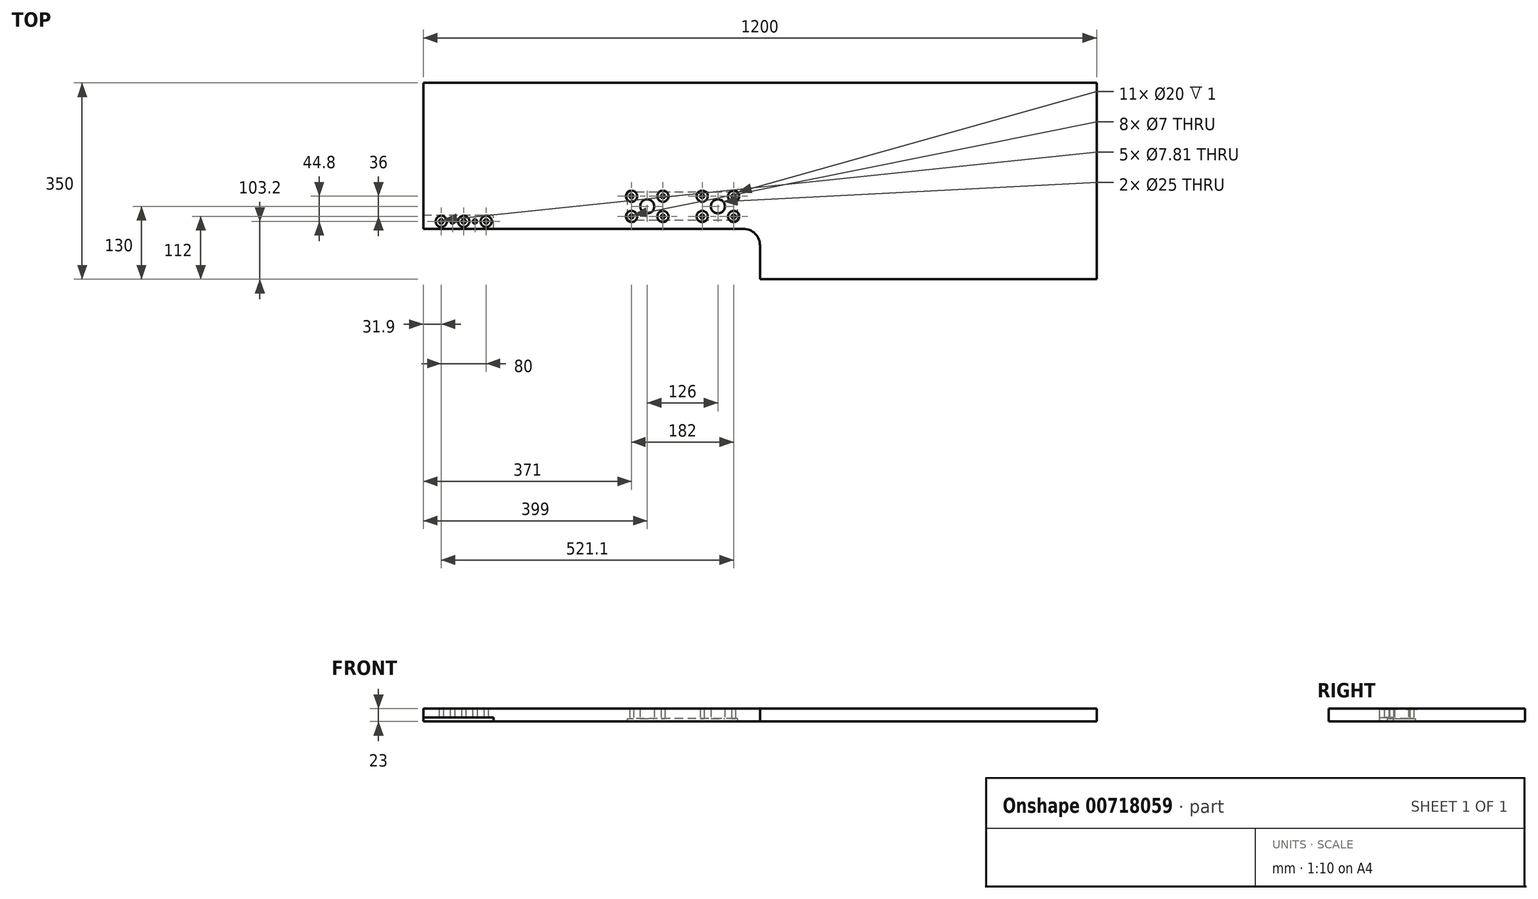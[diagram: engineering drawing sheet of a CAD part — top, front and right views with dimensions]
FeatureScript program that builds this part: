
annotation { "Feature Type Name" : "Feature", "Feature Type Description" : "" }
export const myFeature = defineFeature(function(context is Context, id is Id, definition is map)
    precondition{}
    {
        {
            var Q0;
            Q0=qCreatedBy(makeId("Top.planeOp"),FACE);
            var sketch = newSketch(context, id + "F0", { "sketchPlane" : qUnion([Q0])});
            skLineSegment(sketch, "E0.bottom", {"start": v(600, 0) * mm, "end": v(1200, 0) * mm});
            skLineSegment(sketch, "E0.top", {"start": v(0, 350) * mm, "end": v(1200, 350) * mm});
            skLineSegment(sketch, "E0.right", {"start": v(1200, 0) * mm, "end": v(1200, 350) * mm});
            skLineSegment(sketch, "E1.top", {"start": v(0, 90) * mm, "end": v(570, 90) * mm});
            skLineSegment(sketch, "E1.right", {"start": v(600, 0) * mm, "end": v(600, 60) * mm});
            skLineSegment(sketch, "E2", {"start": v(0, 90) * mm, "end": v(0, 350) * mm});
            skLineSegment(sketch, "E3", {"start": v(0, 0) * mm, "end": v(600, 0) * mm, "construction": true});
            skLineSegment(sketch, "E4", {"start": v(0, 0) * mm, "end": v(0, 90) * mm, "construction": true});
            skPoint(sketch, "E5.visualSharp", {"position": v(600, 90) * mm});
            skArc(sketch, "E5.filletArc", {"start": v(600, 60) * mm, "mid": v(591.21, 81.21) * mm, "end": v(570, 90) * mm});
            skSolve(sketch);
        }
        {
            var Q0;
            Q0=qSketchRegion(id+"F0",true);
            var Q1;
            Q1=makeQuery(id+"F0.imprint","IMPRINT",FACE,{"disambiguationData":[TD([[makeQuery(id+"F0.imprint","IMPRINT",EDGE,{"derivedFrom":sQuery(id+"F0.wireOp",EDGE,"E0.bottom")}),1.0]])]});
            extrude(context, id + "F1", {"entities" : qUnion([Q0, Q1]), "depth" : 18 * mm, "offsetDistance" : 25 * mm});
        }
        {
            var Q0;
            Q0=makeQuery(id+"F1.opExtrude","CAP_FACE",FACE,{"disambiguationData":[OSD([sQuery(id+"F0.wireOp",EDGE,"E0.bottom"),sQuery(id+"F0.wireOp",EDGE,"E0.top"),sQuery(id+"F0.wireOp",EDGE,"E0.right"),sQuery(id+"F0.wireOp",EDGE,"E1.top"),sQuery(id+"F0.wireOp",EDGE,"E1.right"),sQuery(id+"F0.wireOp",EDGE,"E2"),sQuery(id+"F0.wireOp",EDGE,"E5.filletArc")])],"isStart":true});
            var sketch = newSketch(context, id + "F2", { "sketchPlane" : qUnion([Q0])});
            skLineSegment(sketch, "E6.bottom", {"start": v(555, -105) * mm, "end": v(369, -105) * mm});
            skLineSegment(sketch, "E6.top", {"start": v(555, -155) * mm, "end": v(369, -155) * mm});
            skLineSegment(sketch, "E6.left", {"start": v(560, -110) * mm, "end": v(560, -150) * mm});
            skLineSegment(sketch, "E6.right", {"start": v(364, -110) * mm, "end": v(364, -150) * mm});
            skPoint(sketch, "E7.visualSharp", {"position": v(560, -155) * mm});
            skArc(sketch, "E7.filletArc", {"start": v(555, -155) * mm, "mid": v(558.54, -153.54) * mm, "end": v(560, -150) * mm});
            skPoint(sketch, "E8.visualSharp", {"position": v(364, -155) * mm});
            skArc(sketch, "E8.filletArc", {"start": v(364, -150) * mm, "mid": v(365.46, -153.54) * mm, "end": v(369, -155) * mm});
            skPoint(sketch, "E9.visualSharp", {"position": v(364, -105) * mm});
            skArc(sketch, "E9.filletArc", {"start": v(369, -105) * mm, "mid": v(365.46, -106.46) * mm, "end": v(364, -110) * mm});
            skPoint(sketch, "E10.visualSharp", {"position": v(560, -105) * mm});
            skArc(sketch, "E10.filletArc", {"start": v(560, -110) * mm, "mid": v(558.54, -106.46) * mm, "end": v(555, -105) * mm});
            skSolve(sketch);
        }
        {
            var Q0;
            Q0=makeQuery(id+"F2.imprint","IMPRINT",FACE,{"disambiguationData":[TD([[makeQuery(id+"F2.imprint","IMPRINT",EDGE,{"derivedFrom":sQuery(id+"F2.wireOp",EDGE,"E6.bottom")}),-1.0]])]});
            extrude(context, id + "F3", {"entities" : qUnion([Q0]), "operationType" : NewBodyOperationType.ADD, "depth" : 5 * mm, "offsetDistance" : 25 * mm});
        }
        {
            var Q0;
            Q0=makeQuery(id+"F3.opExtrude","CAP_FACE",FACE,{"disambiguationData":[OSD([sQuery(id+"F0.wireOp",EDGE,"E0.bottom"),sQuery(id+"F0.wireOp",EDGE,"E0.top"),sQuery(id+"F0.wireOp",EDGE,"E0.right"),sQuery(id+"F0.wireOp",EDGE,"E1.top"),sQuery(id+"F0.wireOp",EDGE,"E1.right"),sQuery(id+"F0.wireOp",EDGE,"E2"),sQuery(id+"F0.wireOp",EDGE,"E5.filletArc"),sQuery(id+"F2.wireOp",EDGE,"E6.bottom"),sQuery(id+"F2.wireOp",EDGE,"E6.top"),sQuery(id+"F2.wireOp",EDGE,"E6.left"),sQuery(id+"F2.wireOp",EDGE,"E6.right")])],"isStart":false});
            var sketch = newSketch(context, id + "F4", { "sketchPlane" : qUnion([Q0])});
            skLineSegment(sketch, "E11.bottom", {"start": v(0, -90) * mm, "end": v(125, -90) * mm});
            skLineSegment(sketch, "E11.top", {"start": v(0, -114.8) * mm, "end": v(120, -114.8) * mm});
            skLineSegment(sketch, "E11.left", {"start": v(0, -90) * mm, "end": v(0, -114.8) * mm});
            skLineSegment(sketch, "E11.right", {"start": v(125, -90) * mm, "end": v(125, -109.8) * mm});
            skPoint(sketch, "E12.visualSharp", {"position": v(125, -114.8) * mm});
            skArc(sketch, "E12.filletArc", {"start": v(120, -114.8) * mm, "mid": v(123.54, -113.34) * mm, "end": v(125, -109.8) * mm});
            skSolve(sketch);
        }
        {
            var Q0;
            Q0=makeQuery(id+"F4.imprint","IMPRINT",FACE,{"disambiguationData":[TD([[makeQuery(id+"F4.imprint","IMPRINT",EDGE,{"derivedFrom":sQuery(id+"F4.wireOp",EDGE,"E11.bottom")}),-1.0]])]});
            extrude(context, id + "F5", {"entities" : qUnion([Q0]), "operationType" : NewBodyOperationType.REMOVE, "oppositeDirection" : true, "depth" : 7 * mm, "offsetDistance" : 25 * mm});
        }
        {
            var Q0;
            Q0=makeQuery(id+"F1.opExtrude","CAP_FACE",FACE,{"disambiguationData":[OSD([sQuery(id+"F0.wireOp",EDGE,"E0.bottom"),sQuery(id+"F0.wireOp",EDGE,"E0.top"),sQuery(id+"F0.wireOp",EDGE,"E0.right"),sQuery(id+"F0.wireOp",EDGE,"E1.top"),sQuery(id+"F0.wireOp",EDGE,"E1.right"),sQuery(id+"F0.wireOp",EDGE,"E2"),sQuery(id+"F0.wireOp",EDGE,"E5.filletArc")])],"isStart":true});
            var sketch = newSketch(context, id + "F6", { "sketchPlane" : qUnion([Q0])});
            skCircle(sketch, "E13", {"center": v(525, -130) * mm, "radius": 12.5 * mm});
            skCircle(sketch, "E14", {"center": v(399, -130) * mm, "radius": 12.5 * mm});
            skLineSegment(sketch, "E15", {"start": v(399, -130) * mm, "end": v(525, -130) * mm, "construction": true});
            skLineSegment(sketch, "E16.bottom", {"start": v(427, -112) * mm, "end": v(371, -112) * mm, "construction": true});
            skLineSegment(sketch, "E16.top", {"start": v(427, -148) * mm, "end": v(371, -148) * mm, "construction": true});
            skLineSegment(sketch, "E16.left", {"start": v(427, -112) * mm, "end": v(427, -148) * mm, "construction": true});
            skLineSegment(sketch, "E16.right", {"start": v(371, -112) * mm, "end": v(371, -148) * mm, "construction": true});
            skLineSegment(sketch, "E17.bottom", {"start": v(553, -112) * mm, "end": v(497, -112) * mm, "construction": true});
            skLineSegment(sketch, "E17.top", {"start": v(553, -148) * mm, "end": v(497, -148) * mm, "construction": true});
            skLineSegment(sketch, "E17.left", {"start": v(553, -112) * mm, "end": v(553, -148) * mm, "construction": true});
            skLineSegment(sketch, "E17.right", {"start": v(497, -112) * mm, "end": v(497, -148) * mm, "construction": true});
            skCircle(sketch, "E18", {"center": v(371, -112) * mm, "radius": 3.5 * mm});
            skCircle(sketch, "E19", {"center": v(427, -112) * mm, "radius": 3.5 * mm});
            skCircle(sketch, "E20", {"center": v(371, -148) * mm, "radius": 3.5 * mm});
            skCircle(sketch, "E21", {"center": v(427, -148) * mm, "radius": 3.5 * mm});
            skCircle(sketch, "E22", {"center": v(497, -148) * mm, "radius": 3.5 * mm});
            skCircle(sketch, "E23", {"center": v(497, -112) * mm, "radius": 3.5 * mm});
            skCircle(sketch, "E24", {"center": v(553, -112) * mm, "radius": 3.5 * mm});
            skCircle(sketch, "E25", {"center": v(553, -148) * mm, "radius": 3.5 * mm});
            skSolve(sketch);
        }
        {
            var Q0;
            Q0=qSketchRegion(id+"F6",true);
            extrude(context, id + "F7", {"entities" : qUnion([Q0]), "operationType" : NewBodyOperationType.REMOVE, "oppositeDirection" : true, "depth" : 25 * mm, "offsetDistance" : 25 * mm});
        }
        {
            var Q0;
            Q0=makeQuery(id+"F1.opExtrude","CAP_FACE",FACE,{"disambiguationData":[OSD([sQuery(id+"F0.wireOp",EDGE,"E0.bottom"),sQuery(id+"F0.wireOp",EDGE,"E0.top"),sQuery(id+"F0.wireOp",EDGE,"E0.right"),sQuery(id+"F0.wireOp",EDGE,"E1.top"),sQuery(id+"F0.wireOp",EDGE,"E1.right"),sQuery(id+"F0.wireOp",EDGE,"E2"),sQuery(id+"F0.wireOp",EDGE,"E5.filletArc")])],"isStart":false});
            var sketch = newSketch(context, id + "F8", { "sketchPlane" : qUnion([Q0])});
            skCircle(sketch, "E26", {"center": v(371, 148) * mm, "radius": 10 * mm});
            skCircle(sketch, "E27", {"center": v(371, 112) * mm, "radius": 10 * mm});
            skCircle(sketch, "E28", {"center": v(427, 148) * mm, "radius": 10 * mm});
            skCircle(sketch, "E29", {"center": v(427, 112) * mm, "radius": 10 * mm});
            skCircle(sketch, "E30", {"center": v(497, 148) * mm, "radius": 10 * mm});
            skCircle(sketch, "E31", {"center": v(553, 148) * mm, "radius": 10 * mm});
            skCircle(sketch, "E32", {"center": v(553, 112) * mm, "radius": 10 * mm});
            skCircle(sketch, "E33", {"center": v(497, 112) * mm, "radius": 10 * mm});
            skSolve(sketch);
        }
        {
            var Q0;
            Q0=makeQuery(id+"F8.imprint","IMPRINT",FACE,{"disambiguationData":[TD([[makeQuery(id+"F8.imprint","IMPRINT",EDGE,{"derivedFrom":sQuery(id+"F8.wireOp",EDGE,"E26")}),1.0]])]});
            var Q1;
            Q1=makeQuery(id+"F8.imprint","IMPRINT",FACE,{"disambiguationData":[TD([[makeQuery(id+"F8.imprint","IMPRINT",EDGE,{"derivedFrom":sQuery(id+"F8.wireOp",EDGE,"E28")}),1.0]])]});
            var Q2;
            Q2=makeQuery(id+"F8.imprint","IMPRINT",FACE,{"disambiguationData":[TD([[makeQuery(id+"F8.imprint","IMPRINT",EDGE,{"derivedFrom":sQuery(id+"F8.wireOp",EDGE,"E30")}),1.0]])]});
            var Q3;
            Q3=makeQuery(id+"F8.imprint","IMPRINT",FACE,{"disambiguationData":[TD([[makeQuery(id+"F8.imprint","IMPRINT",EDGE,{"derivedFrom":sQuery(id+"F8.wireOp",EDGE,"E31")}),1.0]])]});
            var Q4;
            Q4=makeQuery(id+"F8.imprint","IMPRINT",FACE,{"disambiguationData":[TD([[makeQuery(id+"F8.imprint","IMPRINT",EDGE,{"derivedFrom":sQuery(id+"F8.wireOp",EDGE,"E32")}),1.0]])]});
            var Q5;
            Q5=makeQuery(id+"F8.imprint","IMPRINT",FACE,{"disambiguationData":[TD([[makeQuery(id+"F8.imprint","IMPRINT",EDGE,{"derivedFrom":sQuery(id+"F8.wireOp",EDGE,"E33")}),1.0]])]});
            var Q6;
            Q6=makeQuery(id+"F8.imprint","IMPRINT",FACE,{"disambiguationData":[TD([[makeQuery(id+"F8.imprint","IMPRINT",EDGE,{"derivedFrom":sQuery(id+"F8.wireOp",EDGE,"E29")}),1.0]])]});
            var Q7;
            Q7=makeQuery(id+"F8.imprint","IMPRINT",FACE,{"disambiguationData":[TD([[makeQuery(id+"F8.imprint","IMPRINT",EDGE,{"derivedFrom":sQuery(id+"F8.wireOp",EDGE,"E27")}),1.0]])]});
            extrude(context, id + "F9", {"entities" : qUnion([Q0, Q1, Q2, Q3, Q4, Q5, Q6, Q7]), "operationType" : NewBodyOperationType.REMOVE, "oppositeDirection" : true, "depth" : 1 * mm, "offsetDistance" : 25 * mm});
        }
        {
            var Q0;
            Q0=makeQuery(id+"F5.boolean.opBoolean","COPY",FACE,{"derivedFrom":makeQuery(id+"F5.opExtrude","CAP_FACE",FACE,{"disambiguationData":[OSD([sQuery(id+"F4.wireOp",EDGE,"E11.bottom"),sQuery(id+"F4.wireOp",EDGE,"E11.top"),sQuery(id+"F4.wireOp",EDGE,"E11.left"),sQuery(id+"F4.wireOp",EDGE,"E11.right"),sQuery(id+"F4.wireOp",EDGE,"E12.filletArc")])],"isStart":false})});
            var sketch = newSketch(context, id + "F10", { "sketchPlane" : qUnion([Q0])});
            skCircle(sketch, "E34", {"center": v(111.9, -103.2) * mm, "radius": 3.9 * mm});
            skCircle(sketch, "E35", {"center": v(91.9, -103.2) * mm, "radius": 3.9 * mm});
            skCircle(sketch, "E36", {"center": v(71.9, -103.2) * mm, "radius": 3.9 * mm});
            skCircle(sketch, "E37", {"center": v(51.9, -103.2) * mm, "radius": 3.9 * mm});
            skCircle(sketch, "E38", {"center": v(31.9, -103.2) * mm, "radius": 3.9 * mm});
            skLineSegment(sketch, "E39", {"start": v(111.9, -103.2) * mm, "end": v(91.9, -103.2) * mm, "construction": true});
            skLineSegment(sketch, "E40", {"start": v(91.9, -103.2) * mm, "end": v(71.9, -103.2) * mm, "construction": true});
            skLineSegment(sketch, "E41", {"start": v(71.9, -103.2) * mm, "end": v(51.9, -103.2) * mm, "construction": true});
            skLineSegment(sketch, "E42", {"start": v(51.9, -103.2) * mm, "end": v(31.9, -103.2) * mm, "construction": true});
            skSolve(sketch);
        }
        {
            var Q0;
            Q0=qSketchRegion(id+"F10",true);
            extrude(context, id + "F11", {"entities" : qUnion([Q0]), "operationType" : NewBodyOperationType.REMOVE, "oppositeDirection" : true, "depth" : 25 * mm, "offsetDistance" : 25 * mm});
        }
        {
            var Q0;
            Q0=makeQuery(id+"F1.opExtrude","CAP_FACE",FACE,{"disambiguationData":[OSD([sQuery(id+"F0.wireOp",EDGE,"E0.bottom"),sQuery(id+"F0.wireOp",EDGE,"E0.top"),sQuery(id+"F0.wireOp",EDGE,"E0.right"),sQuery(id+"F0.wireOp",EDGE,"E1.top"),sQuery(id+"F0.wireOp",EDGE,"E1.right"),sQuery(id+"F0.wireOp",EDGE,"E2"),sQuery(id+"F0.wireOp",EDGE,"E5.filletArc")])],"isStart":false});
            var sketch = newSketch(context, id + "F12", { "sketchPlane" : qUnion([Q0])});
            skCircle(sketch, "E43", {"center": v(111.9, 103.2) * mm, "radius": 10 * mm});
            skCircle(sketch, "E44", {"center": v(71.9, 103.2) * mm, "radius": 10 * mm});
            skCircle(sketch, "E45", {"center": v(31.9, 103.2) * mm, "radius": 10 * mm});
            skSolve(sketch);
        }
        {
            var Q0;
            Q0=makeQuery(id+"F12.imprint","IMPRINT",FACE,{"disambiguationData":[TD([[makeQuery(id+"F12.imprint","IMPRINT",EDGE,{"derivedFrom":sQuery(id+"F12.wireOp",EDGE,"E45")}),1.0]])]});
            var Q1;
            Q1=makeQuery(id+"F12.imprint","IMPRINT",FACE,{"disambiguationData":[TD([[makeQuery(id+"F12.imprint","IMPRINT",EDGE,{"derivedFrom":sQuery(id+"F12.wireOp",EDGE,"E44")}),1.0]])]});
            var Q2;
            Q2=makeQuery(id+"F12.imprint","IMPRINT",FACE,{"disambiguationData":[TD([[makeQuery(id+"F12.imprint","IMPRINT",EDGE,{"derivedFrom":sQuery(id+"F12.wireOp",EDGE,"E43")}),1.0]])]});
            extrude(context, id + "F13", {"entities" : qUnion([Q0, Q1, Q2]), "operationType" : NewBodyOperationType.REMOVE, "oppositeDirection" : true, "depth" : 1 * mm, "offsetDistance" : 25 * mm});
        }
    });
